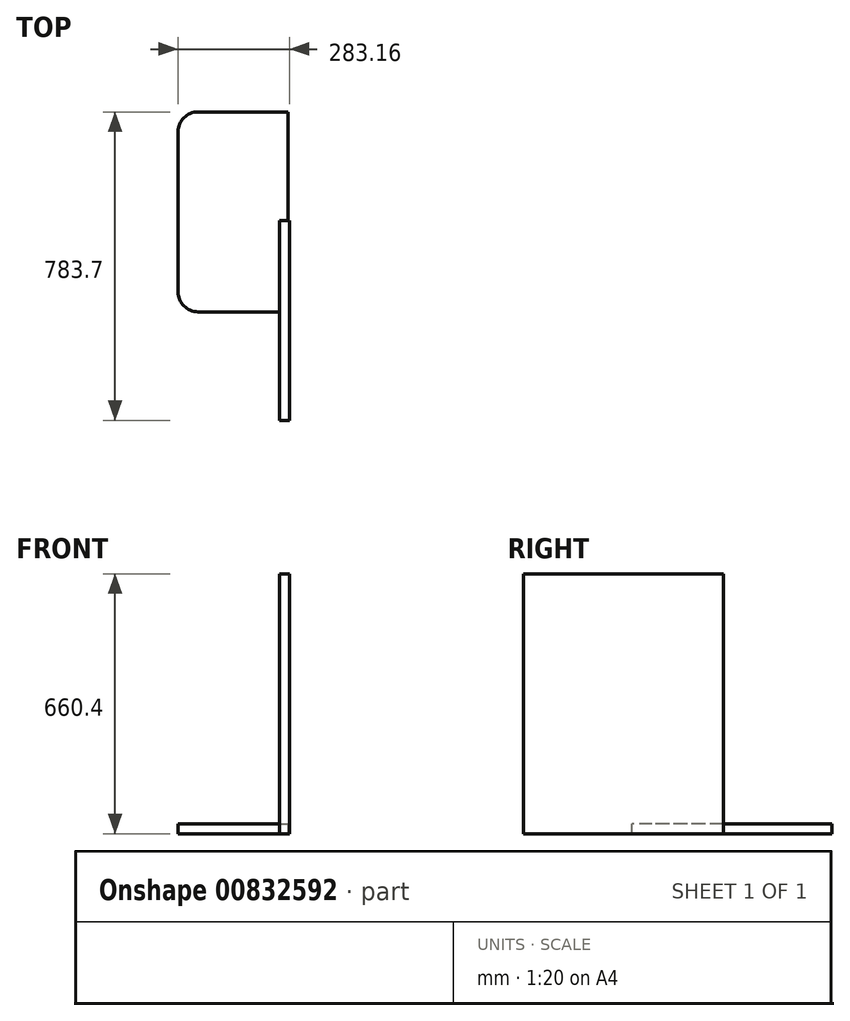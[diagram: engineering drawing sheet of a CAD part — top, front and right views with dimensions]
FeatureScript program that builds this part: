
annotation { "Feature Type Name" : "Feature", "Feature Type Description" : "" }
export const myFeature = defineFeature(function(context is Context, id is Id, definition is map)
    precondition{}
    {
        {
            var Q0;
            Q0=qCreatedBy(makeId("Top.planeOp"),FACE);
            var sketch = newSketch(context, id + "F0", { "sketchPlane" : qUnion([Q0])});
            skLineSegment(sketch, "E0.bottom", {"start": v(-206.96, 211.57) * mm, "end": v(21.64, 211.57) * mm});
            skLineSegment(sketch, "E0.top", {"start": v(-206.96, -296.43) * mm, "end": v(21.64, -296.43) * mm});
            skLineSegment(sketch, "E0.left", {"start": v(-257.76, 160.77) * mm, "end": v(-257.76, -245.63) * mm});
            skLineSegment(sketch, "E0.right", {"start": v(21.64, 211.57) * mm, "end": v(21.64, -296.43) * mm});
            skPoint(sketch, "E1.visualSharp", {"position": v(-257.76, -296.43) * mm});
            skArc(sketch, "E1.filletArc", {"start": v(-257.76, -245.63) * mm, "mid": v(-242.89, -281.56) * mm, "end": v(-206.96, -296.43) * mm});
            skPoint(sketch, "E2.visualSharp", {"position": v(-257.76, 211.57) * mm});
            skArc(sketch, "E2.filletArc", {"start": v(-206.96, 211.57) * mm, "mid": v(-242.89, 196.69) * mm, "end": v(-257.76, 160.77) * mm});
            skSolve(sketch);
        }
        {
            var Q0;
            Q0=qCreatedBy(makeId("Right.planeOp"),FACE);
            var sketch = newSketch(context, id + "F1", { "sketchPlane" : qUnion([Q0])});
            skLineSegment(sketch, "E3.bottom", {"start": v(-572.13, 660.4) * mm, "end": v(-64.13, 660.4) * mm});
            skLineSegment(sketch, "E3.top", {"start": v(-572.13, 0) * mm, "end": v(-64.13, 0) * mm});
            skLineSegment(sketch, "E3.left", {"start": v(-572.13, 660.4) * mm, "end": v(-572.13, 0) * mm});
            skLineSegment(sketch, "E3.right", {"start": v(-64.13, 660.4) * mm, "end": v(-64.13, 0) * mm});
            skSolve(sketch);
        }
        {
            var Q0;
            Q0=makeQuery(id+"F1.imprint","IMPRINT",FACE,{"disambiguationData":[TD([[makeQuery(id+"F1.imprint","IMPRINT",EDGE,{"derivedFrom":sQuery(id+"F1.wireOp",EDGE,"E3.bottom")}),-1.0]])]});
            extrude(context, id + "F2", {"entities" : qUnion([Q0]), "depth" : 25.4 * mm, "offsetDistance" : 25 * mm});
        }
        {
            var Q0;
            Q0=makeQuery(id+"F0.imprint","IMPRINT",FACE,{"disambiguationData":[TD([[makeQuery(id+"F0.imprint","IMPRINT",EDGE,{"derivedFrom":sQuery(id+"F0.wireOp",EDGE,"E0.bottom")}),-1.0]])]});
            extrude(context, id + "F3", {"entities" : qUnion([Q0]), "operationType" : NewBodyOperationType.ADD, "depth" : 25.4 * mm, "offsetDistance" : 25 * mm});
        }
    });
